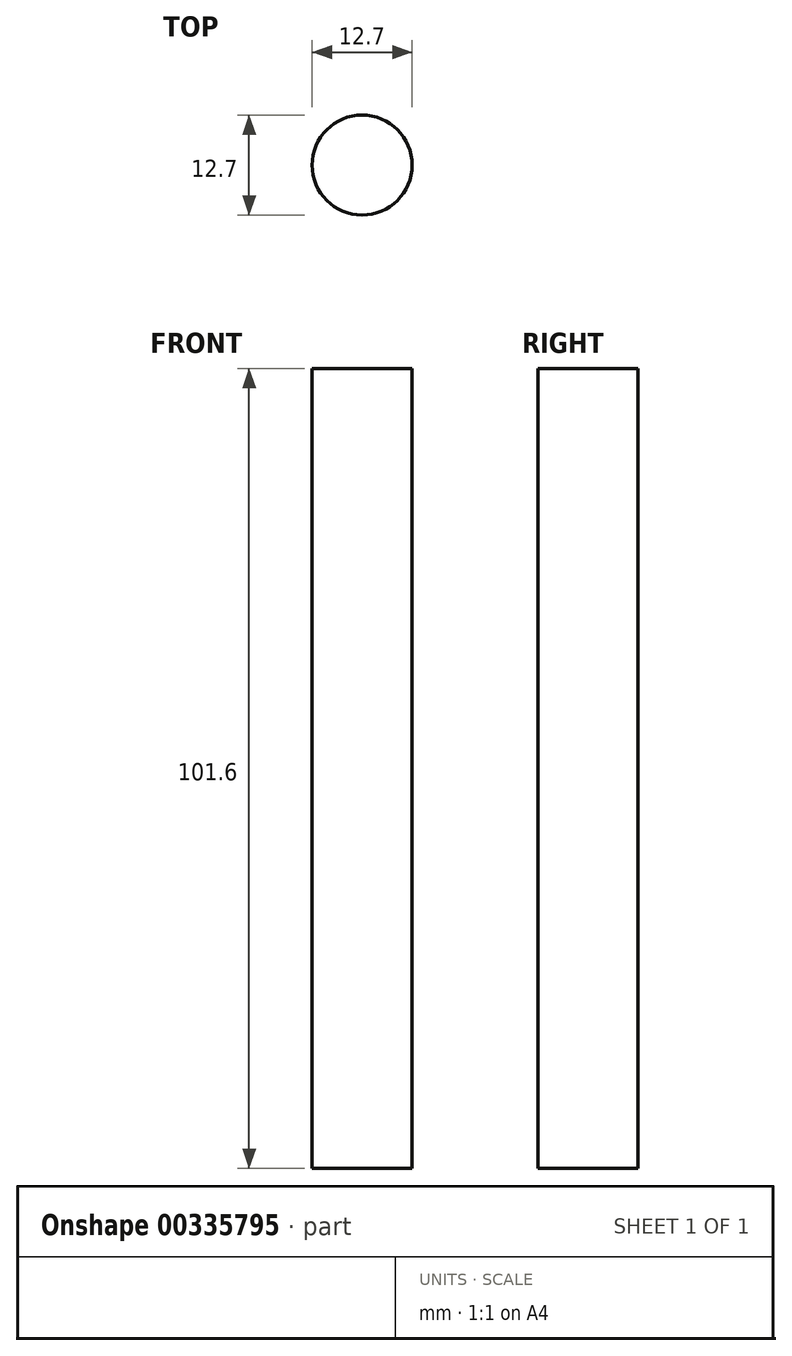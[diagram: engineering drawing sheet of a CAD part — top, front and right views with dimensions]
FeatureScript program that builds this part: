
annotation { "Feature Type Name" : "Feature", "Feature Type Description" : "" }
export const myFeature = defineFeature(function(context is Context, id is Id, definition is map)
    precondition{}
    {
        {
            var Q0;
            Q0=qCreatedBy(makeId("Top.planeOp"),FACE);
            var sketch = newSketch(context, id + "F0", { "sketchPlane" : qUnion([Q0])});
            skCircle(sketch, "E0", {"center": v(-69.33, 12.44) * mm, "radius": 1.4 * mm});
            skLineSegment(sketch, "E1.bottom", {"start": v(-58.64, 10.52) * mm, "end": v(-54.07, 10.52) * mm});
            skLineSegment(sketch, "E1.top", {"start": v(-58.64, 7.82) * mm, "end": v(-54.07, 7.82) * mm});
            skLineSegment(sketch, "E1.left", {"start": v(-58.64, 10.52) * mm, "end": v(-58.64, 7.82) * mm});
            skLineSegment(sketch, "E1.right", {"start": v(-54.07, 10.52) * mm, "end": v(-54.07, 7.82) * mm});
            skLineSegment(sketch, "E2", {"start": v(-68.42, 3.7) * mm, "end": v(-64.16, 2.24) * mm});
            skLineSegment(sketch, "E3", {"start": v(-64.16, 2.24) * mm, "end": v(-64.16, -2.02) * mm});
            skLineSegment(sketch, "E4", {"start": v(-64.16, -2.02) * mm, "end": v(-69.04, -2.8) * mm});
            skLineSegment(sketch, "E5", {"start": v(-69.04, -2.8) * mm, "end": v(-68.42, 3.7) * mm});
            skLineSegment(sketch, "E6", {"start": v(-67.12, 1.88) * mm, "end": v(-67.85, -1.03) * mm});
            skLineSegment(sketch, "E7", {"start": v(-67.85, -1.03) * mm, "end": v(-66.28, -1.42) * mm});
            skLineSegment(sketch, "E8", {"start": v(-66.28, -1.42) * mm, "end": v(-67.12, 1.88) * mm});
            skCircle(sketch, "E9", {"center": v(-80.25, 9.87) * mm, "radius": 6.35 * mm});
            skSolve(sketch);
        }
        {
            var Q0;
            Q0=makeQuery(id+"F0.imprint","IMPRINT",FACE,{"disambiguationData":[TD([[makeQuery(id+"F0.imprint","IMPRINT",EDGE,{"derivedFrom":sQuery(id+"F0.wireOp",EDGE,"E9")}),1.0]])]});
            extrude(context, id + "F1", {"entities" : qUnion([Q0]), "depth" : 101.6 * mm});
        }
    });
